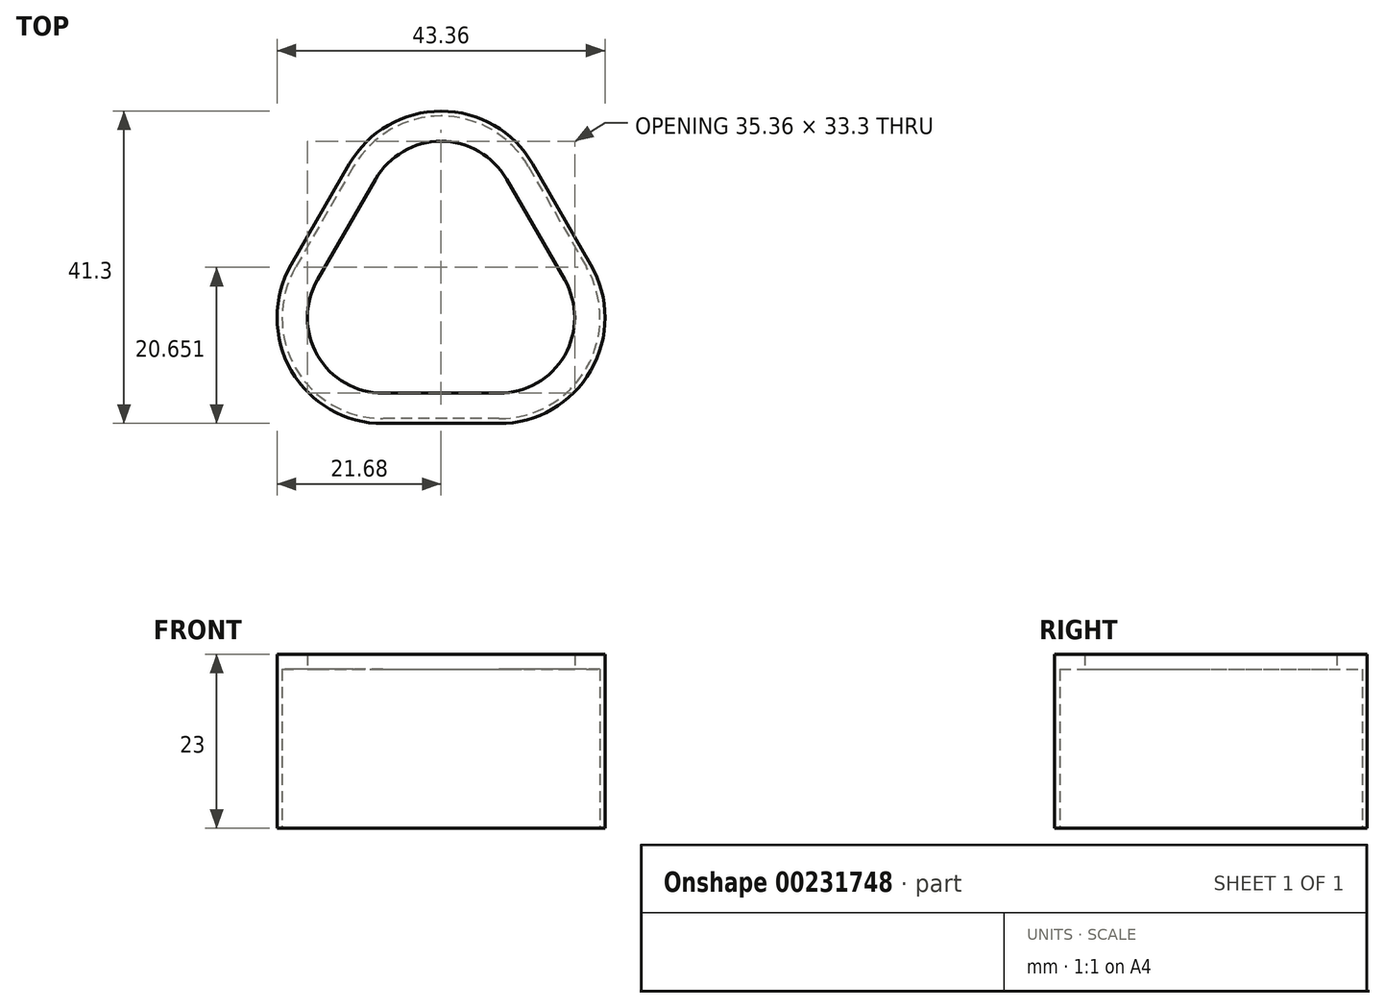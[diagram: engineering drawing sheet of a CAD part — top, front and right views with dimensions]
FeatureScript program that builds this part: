
annotation { "Feature Type Name" : "Feature", "Feature Type Description" : "" }
export const myFeature = defineFeature(function(context is Context, id is Id, definition is map)
    precondition{}
    {
        {
            var Q0;
            Q0=qCreatedBy(makeId("Top.planeOp"),FACE);
            var sketch = newSketch(context, id + "F0", { "sketchPlane" : qUnion([Q0])});
            skLineSegment(sketch, "E0", {"start": v(0, 0) * mm, "end": v(7.68, 0) * mm});
            skLineSegment(sketch, "E1", {"start": v(16.34, 15) * mm, "end": v(8.66, 28.3) * mm});
            skLineSegment(sketch, "E2", {"start": v(-8.66, 28.3) * mm, "end": v(-16.34, 15) * mm});
            skLineSegment(sketch, "E3", {"start": v(-7.68, 0) * mm, "end": v(0, 0) * mm});
            skLineSegment(sketch, "E4", {"start": v(0, 0) * mm, "end": v(0, 43.3) * mm, "construction": true});
            skLineSegment(sketch, "E5", {"start": v(-12.5, 21.65) * mm, "end": v(25, 0) * mm, "construction": true});
            skLineSegment(sketch, "E6", {"start": v(12.5, 21.65) * mm, "end": v(-25, 0) * mm, "construction": true});
            skCircle(sketch, "E7", {"center": v(0, 14.43) * mm, "radius": 12.5 * mm});
            skPoint(sketch, "E8.visualSharp", {"position": v(0, 43.3) * mm});
            skArc(sketch, "E8.filletArc", {"start": v(8.66, 28.3) * mm, "mid": v(0, 33.3) * mm, "end": v(-8.66, 28.3) * mm});
            skPoint(sketch, "E9.visualSharp", {"position": v(-25, 0) * mm});
            skArc(sketch, "E9.filletArc", {"start": v(-16.34, 15) * mm, "mid": v(-16.34, 5) * mm, "end": v(-7.68, 0) * mm});
            skPoint(sketch, "E10.visualSharp", {"position": v(25, 0) * mm});
            skArc(sketch, "E10.filletArc", {"start": v(7.68, 0) * mm, "mid": v(16.34, 5) * mm, "end": v(16.34, 15) * mm});
            skLineSegment(sketch, "E11.0", {"start": v(19.8, 17) * mm, "end": v(12.12, 30.3) * mm});
            skArc(sketch, "E11.1", {"start": v(7.68, -4) * mm, "mid": v(19.8, 3) * mm, "end": v(19.8, 17) * mm});
            skLineSegment(sketch, "E11.2", {"start": v(-12.12, 30.3) * mm, "end": v(-19.8, 17) * mm});
            skArc(sketch, "E11.3", {"start": v(-19.8, 17) * mm, "mid": v(-19.8, 3) * mm, "end": v(-7.68, -4) * mm});
            skLineSegment(sketch, "E11.4", {"start": v(-7.68, -4) * mm, "end": v(0, -4) * mm});
            skArc(sketch, "E11.5", {"start": v(12.12, 30.3) * mm, "mid": v(0, 37.3) * mm, "end": v(-12.12, 30.3) * mm});
            skLineSegment(sketch, "E11.6", {"start": v(0, -4) * mm, "end": v(7.68, -4) * mm});
            skSolve(sketch);
        }
        {
            var Q0;
            Q0=makeQuery(id+"F0.imprint","IMPRINT",FACE,{"disambiguationData":[TD([[makeQuery(id+"F0.imprint","IMPRINT",EDGE,{"derivedFrom":sQuery(id+"F0.wireOp",EDGE,"E0")}),-1.0]])]});
            extrude(context, id + "F1", {"entities" : qUnion([Q0]), "depth" : 25 * mm});
        }
        {
            var Q0;
            Q0=makeQuery(id+"F1.opExtrude","SWEPT_FACE",FACE,{"disambiguationData":[OSD([sQuery(id+"F0.wireOp",EDGE,"E11.2")])]});
            var sketch = newSketch(context, id + "F2", { "sketchPlane" : qUnion([Q0])});
            skCircle(sketch, "E12", {"center": v(-12.5, 12.5) * mm, "radius": 4.3 * mm});
            skPoint(sketch, "E12.centerSnap0", {"position": v(-12.5, 25) * mm});
            skPoint(sketch, "E12.centerSnap1", {"position": v(-20.18, 12.5) * mm});
            skSolve(sketch);
        }
        {
            var Q0;
            Q0=qSketchRegion(id+"F2",true);
            extrude(context, id + "F3", {"entities" : qUnion([Q0]), "operationType" : NewBodyOperationType.REMOVE, "oppositeDirection" : true, "depth" : 2.8 * mm, "hasSecondDirection" : true, "secondDirectionOppositeDirection" : true, "secondDirectionDepth" : 0.65 * mm});
        }
        {
            var Q0;
            Q0=makeQuery(id+"F1.opExtrude","CAP_FACE",FACE,{"disambiguationData":[OSD([sQuery(id+"F0.wireOp",EDGE,"E0"),sQuery(id+"F0.wireOp",EDGE,"E1"),sQuery(id+"F0.wireOp",EDGE,"E2"),sQuery(id+"F0.wireOp",EDGE,"E3"),sQuery(id+"F0.wireOp",EDGE,"E8.filletArc"),sQuery(id+"F0.wireOp",EDGE,"E9.filletArc"),sQuery(id+"F0.wireOp",EDGE,"E10.filletArc"),sQuery(id+"F0.wireOp",EDGE,"E11.0"),sQuery(id+"F0.wireOp",EDGE,"E11.1"),sQuery(id+"F0.wireOp",EDGE,"E11.2"),sQuery(id+"F0.wireOp",EDGE,"E11.3"),sQuery(id+"F0.wireOp",EDGE,"E11.4"),sQuery(id+"F0.wireOp",EDGE,"E11.5"),sQuery(id+"F0.wireOp",EDGE,"E11.6")])],"isStart":false});
            var sketch = newSketch(context, id + "F4", { "sketchPlane" : qUnion([Q0])});
            skLineSegment(sketch, "E13", {"start": v(-12.5, 21.65) * mm, "end": v(16.34, 5) * mm});
            skLineSegment(sketch, "E14", {"start": v(16.34, 5) * mm, "end": v(0, 0) * mm});
            skLineSegment(sketch, "E15", {"start": v(0, 0) * mm, "end": v(0, 33.3) * mm});
            skCircle(sketch, "E16", {"center": v(0, 14.43) * mm, "radius": 3.2 * mm});
            skSolve(sketch);
        }
        {
            var Q0;
            Q0=makeQuery(id+"F1.opExtrude","CAP_FACE",FACE,{"disambiguationData":[OSD([sQuery(id+"F0.wireOp",EDGE,"E0"),sQuery(id+"F0.wireOp",EDGE,"E1"),sQuery(id+"F0.wireOp",EDGE,"E2"),sQuery(id+"F0.wireOp",EDGE,"E3"),sQuery(id+"F0.wireOp",EDGE,"E8.filletArc"),sQuery(id+"F0.wireOp",EDGE,"E9.filletArc"),sQuery(id+"F0.wireOp",EDGE,"E10.filletArc"),sQuery(id+"F0.wireOp",EDGE,"E11.0"),sQuery(id+"F0.wireOp",EDGE,"E11.1"),sQuery(id+"F0.wireOp",EDGE,"E11.2"),sQuery(id+"F0.wireOp",EDGE,"E11.3"),sQuery(id+"F0.wireOp",EDGE,"E11.4"),sQuery(id+"F0.wireOp",EDGE,"E11.5"),sQuery(id+"F0.wireOp",EDGE,"E11.6")])],"isStart":true});
            var sketch = newSketch(context, id + "F5", { "sketchPlane" : qUnion([Q0])});
            skLineSegment(sketch, "E17.0", {"start": v(-11.56, -29.98) * mm, "end": v(-19.24, -16.67) * mm});
            skLineSegment(sketch, "E17.1", {"start": v(-7.68, 3.35) * mm, "end": v(7.68, 3.35) * mm});
            skArc(sketch, "E17.2", {"start": v(7.68, 3.35) * mm, "mid": v(19.24, -3.33) * mm, "end": v(19.24, -16.68) * mm});
            skArc(sketch, "E17.3", {"start": v(-19.24, -16.67) * mm, "mid": v(-19.24, -3.32) * mm, "end": v(-7.68, 3.35) * mm});
            skLineSegment(sketch, "E17.4", {"start": v(19.24, -16.67) * mm, "end": v(11.56, -29.98) * mm});
            skArc(sketch, "E17.5", {"start": v(11.56, -29.98) * mm, "mid": v(0, -36.65) * mm, "end": v(-11.56, -29.98) * mm});
            skSolve(sketch);
        }
        {
            var Q0;
            Q0 = qSketchRegion(id + "F5", true);
            extrude(context, id + "F6", {"entities" : qUnion([Q0]), "operationType" : NewBodyOperationType.REMOVE, "oppositeDirection" : true, "depth" : 23 * mm});
        }
        {
            var Q0;
            Q0=makeQuery(id+"F1.opExtrude","CAP_FACE",FACE,{"disambiguationData":[OSD([sQuery(id+"F0.wireOp",EDGE,"E0"),sQuery(id+"F0.wireOp",EDGE,"E1"),sQuery(id+"F0.wireOp",EDGE,"E2"),sQuery(id+"F0.wireOp",EDGE,"E3"),sQuery(id+"F0.wireOp",EDGE,"E8.filletArc"),sQuery(id+"F0.wireOp",EDGE,"E9.filletArc"),sQuery(id+"F0.wireOp",EDGE,"E10.filletArc"),sQuery(id+"F0.wireOp",EDGE,"E11.0"),sQuery(id+"F0.wireOp",EDGE,"E11.1"),sQuery(id+"F0.wireOp",EDGE,"E11.2"),sQuery(id+"F0.wireOp",EDGE,"E11.3"),sQuery(id+"F0.wireOp",EDGE,"E11.4"),sQuery(id+"F0.wireOp",EDGE,"E11.5"),sQuery(id+"F0.wireOp",EDGE,"E11.6")])],"isStart":true});
            var sketch = newSketch(context, id + "F7", { "sketchPlane" : qUnion([Q0])});
            skCircle(sketch, "E18", {"center": v(-1.2, -16.8) * mm, "radius": 33.55 * mm});
            skSolve(sketch);
        }
        {
            var Q0;
            Q0 = qSketchRegion(id + "F7", true);
            extrude(context, id + "F8", {"entities" : qUnion([Q0]), "operationType" : NewBodyOperationType.REMOVE, "oppositeDirection" : true, "depth" : 2 * mm});
        }
    });
